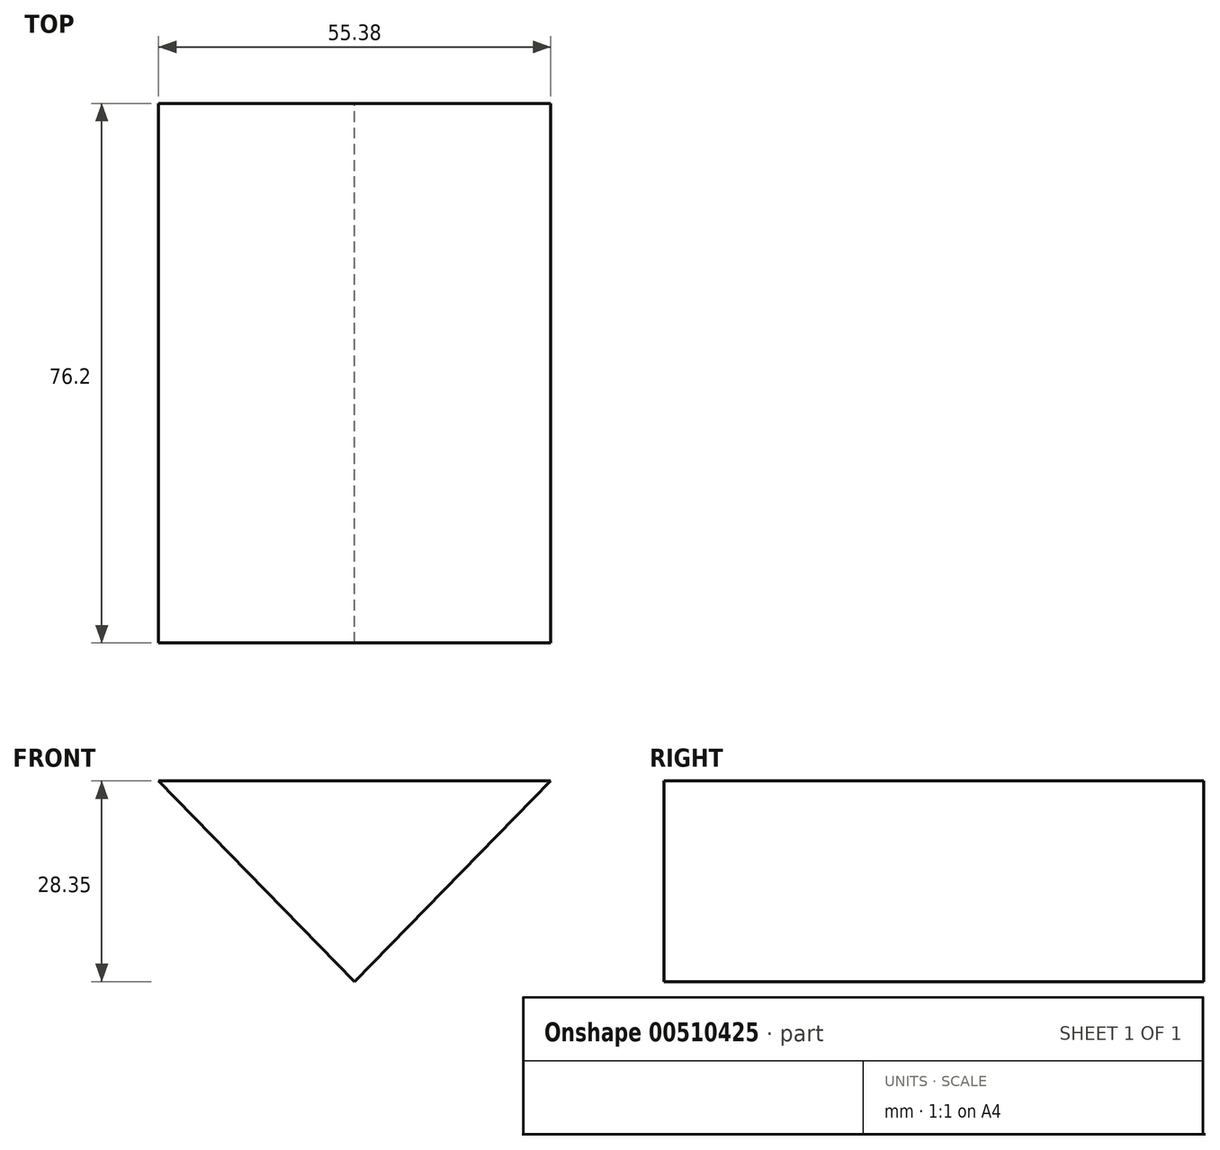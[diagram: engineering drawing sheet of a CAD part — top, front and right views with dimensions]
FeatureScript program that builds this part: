
annotation { "Feature Type Name" : "Feature", "Feature Type Description" : "" }
export const myFeature = defineFeature(function(context is Context, id is Id, definition is map)
    precondition{}
    {
        {
            var Q0;
            Q0=qCreatedBy(makeId("Front.planeOp"),FACE);
            var sketch = newSketch(context, id + "F0", { "sketchPlane" : qUnion([Q0])});
            skLineSegment(sketch, "E0", {"start": v(0, 0) * mm, "end": v(-27.69, 28.35) * mm});
            skLineSegment(sketch, "E1", {"start": v(-27.69, 28.35) * mm, "end": v(27.69, 28.35) * mm});
            skLineSegment(sketch, "E2", {"start": v(27.69, 28.35) * mm, "end": v(0, 0) * mm});
            skSolve(sketch);
        }
        {
            var Q0;
            Q0=makeQuery(id+"F0.imprint","IMPRINT",FACE,{"disambiguationData":[TD([[makeQuery(id+"F0.imprint","IMPRINT",EDGE,{"derivedFrom":sQuery(id+"F0.wireOp",EDGE,"E0")}),-1.0]])]});
            extrude(context, id + "F1", {"entities" : qUnion([Q0]), "depth" : 76.2 * mm});
        }
    });
